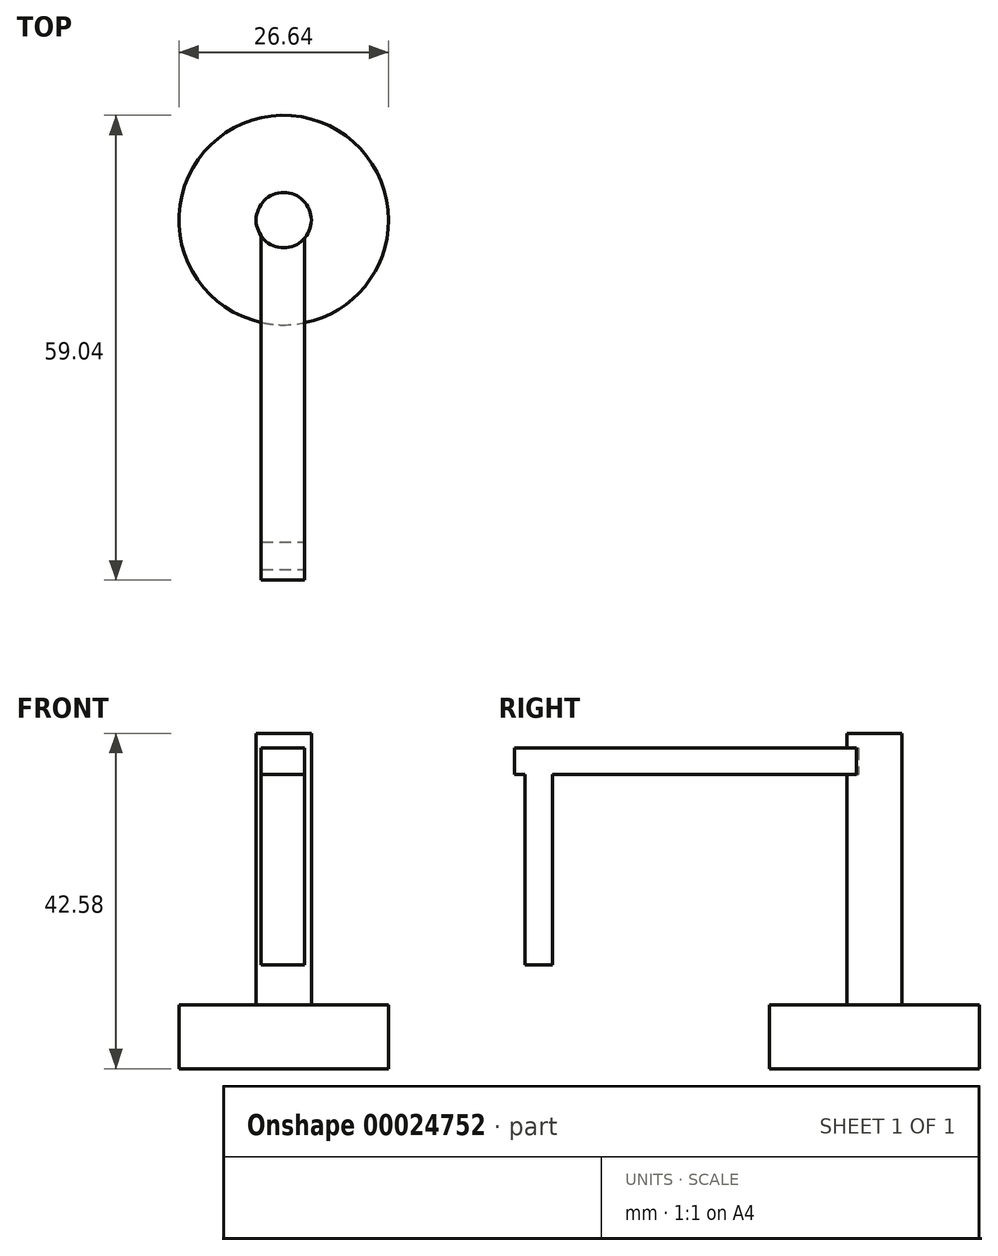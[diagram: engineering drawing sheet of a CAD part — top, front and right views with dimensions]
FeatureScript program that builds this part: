
annotation { "Feature Type Name" : "Feature", "Feature Type Description" : "" }
export const myFeature = defineFeature(function(context is Context, id is Id, definition is map)
    precondition{}
    {
        {
            var Q0;
            Q0=qCreatedBy(makeId("Top.planeOp"),FACE);
            var sketch = newSketch(context, id + "F0", { "sketchPlane" : qUnion([Q0])});
            skCircle(sketch, "E0", {"center": v(0, 0) * mm, "radius": 13.32 * mm});
            skSolve(sketch);
        }
        {
            var Q0;
            Q0=makeQuery(id+"F0.imprint","IMPRINT",FACE,{"disambiguationData":[TD([[makeQuery(id+"F0.imprint","IMPRINT",EDGE,{"derivedFrom":sQuery(id+"F0.wireOp",EDGE,"E0")}),1.0]])]});
            extrude(context, id + "F1", {"entities" : qUnion([Q0]), "depth" : 8.12 * mm});
        }
        {
            var Q0;
            Q0=makeQuery(id+"F1.opExtrude","CAP_FACE",FACE,{"disambiguationData":[OSD([sQuery(id+"F0.wireOp",EDGE,"E0")])],"isStart":false});
            var sketch = newSketch(context, id + "F2", { "sketchPlane" : qUnion([Q0])});
            skCircle(sketch, "E1", {"center": v(0, 0) * mm, "radius": 3.5 * mm});
            skSolve(sketch);
        }
        {
            var Q0;
            Q0 = qSketchRegion(id + "F2", true);
            var Q1;
            Q1 = qSketchRegion(id + "F4", true);
            extrude(context, id + "F3", {"entities" : qUnion([Q0, Q1]), "operationType" : NewBodyOperationType.ADD, "depth" : 34.46 * mm});
        }
        {
            var Q0;
            Q0=qCreatedBy(makeId("Right.planeOp"),FACE);
            var sketch = newSketch(context, id + "F4", { "sketchPlane" : qUnion([Q0])});
            skSolve(sketch);
        }
        {
            var Q0;
            Q0=qCreatedBy(makeId("Front.planeOp"),FACE);
            var sketch = newSketch(context, id + "F5", { "sketchPlane" : qUnion([Q0])});
            skLineSegment(sketch, "E2.bottom", {"start": v(2.67, 40.71) * mm, "end": v(-2.85, 40.71) * mm});
            skLineSegment(sketch, "E2.top", {"start": v(2.67, 37.35) * mm, "end": v(-2.85, 37.35) * mm});
            skLineSegment(sketch, "E2.left", {"start": v(2.67, 40.71) * mm, "end": v(2.67, 37.35) * mm});
            skLineSegment(sketch, "E2.right", {"start": v(-2.85, 40.71) * mm, "end": v(-2.85, 37.35) * mm});
            skSolve(sketch);
        }
        {
            var Q0;
            Q0 = qSketchRegion(id + "F5", true);
            extrude(context, id + "F6", {"entities" : qUnion([Q0]), "operationType" : NewBodyOperationType.ADD, "depth" : 45.72 * mm});
        }
        {
            var Q0;
            Q0=makeQuery(id+"F6.opExtrude","SWEPT_FACE",FACE,{"disambiguationData":[OSD([sQuery(id+"F5.wireOp",EDGE,"E2.top")])]});
            var sketch = newSketch(context, id + "F7", { "sketchPlane" : qUnion([Q0])});
            skLineSegment(sketch, "E3.bottom", {"start": v(-2.85, 44.37) * mm, "end": v(2.67, 44.37) * mm});
            skLineSegment(sketch, "E3.top", {"start": v(-2.85, 40.9) * mm, "end": v(2.67, 40.9) * mm});
            skLineSegment(sketch, "E3.left", {"start": v(-2.85, 44.37) * mm, "end": v(-2.85, 40.9) * mm});
            skLineSegment(sketch, "E3.right", {"start": v(2.67, 44.37) * mm, "end": v(2.67, 40.9) * mm});
            skSolve(sketch);
        }
        {
            var Q0;
            Q0 = qSketchRegion(id + "F7", true);
            extrude(context, id + "F8", {"entities" : qUnion([Q0]), "operationType" : NewBodyOperationType.ADD, "depth" : 24.2 * mm});
        }
    });
